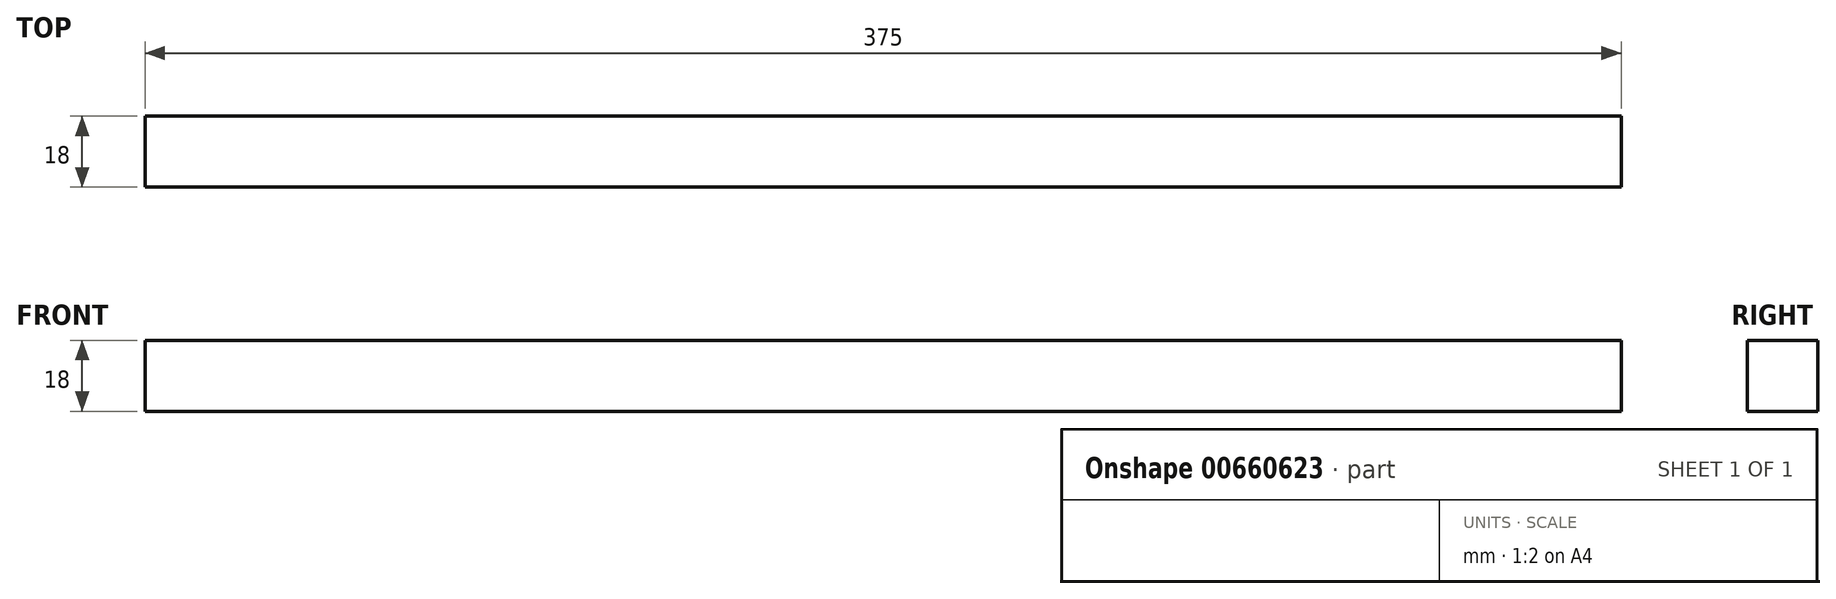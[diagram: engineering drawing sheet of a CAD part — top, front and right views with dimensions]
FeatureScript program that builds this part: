
annotation { "Feature Type Name" : "Feature", "Feature Type Description" : "" }
export const myFeature = defineFeature(function(context is Context, id is Id, definition is map)
    precondition{}
    {
        {
            var Q0;
            Q0=qCreatedBy(makeId("Front.planeOp"),FACE);
            var sketch = newSketch(context, id + "F0", { "sketchPlane" : qUnion([Q0])});
            skLineSegment(sketch, "E0.bottom", {"start": v(-115.54, 22.06) * mm, "end": v(259.46, 22.06) * mm});
            skLineSegment(sketch, "E0.top", {"start": v(-115.54, 4.06) * mm, "end": v(259.46, 4.06) * mm});
            skLineSegment(sketch, "E0.left", {"start": v(-115.54, 22.06) * mm, "end": v(-115.54, 4.06) * mm});
            skLineSegment(sketch, "E0.right", {"start": v(259.46, 22.06) * mm, "end": v(259.46, 4.06) * mm});
            skSolve(sketch);
        }
        {
            var Q0;
            Q0 = qSketchRegion(id + "F0", true);
            extrude(context, id + "F1", {"entities" : qUnion([Q0]), "depth" : 18 * mm, "offsetDistance" : 25 * mm});
        }
    });
